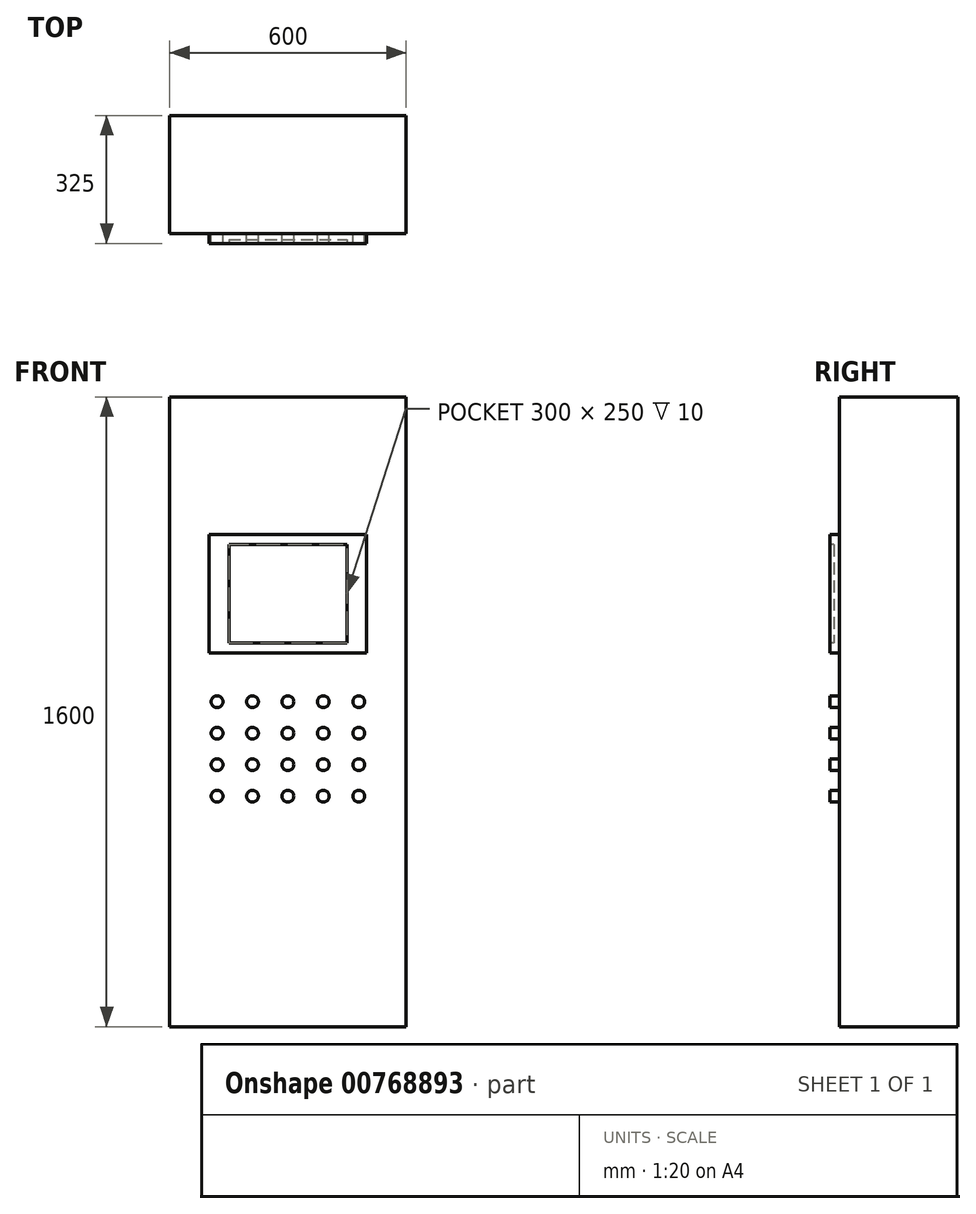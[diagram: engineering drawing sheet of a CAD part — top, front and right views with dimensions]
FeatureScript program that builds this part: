
annotation { "Feature Type Name" : "Feature", "Feature Type Description" : "" }
export const myFeature = defineFeature(function(context is Context, id is Id, definition is map)
    precondition{}
    {
        {
            var Q0;
            Q0=qCreatedBy(makeId("Front.planeOp"),FACE);
            var sketch = newSketch(context, id + "F0", { "sketchPlane" : qUnion([Q0])});
            skLineSegment(sketch, "E0.bottom", {"start": v(0, 0) * mm, "end": v(600, 0) * mm});
            skLineSegment(sketch, "E0.top", {"start": v(0, 1600) * mm, "end": v(600, 1600) * mm});
            skLineSegment(sketch, "E0.left", {"start": v(0, 0) * mm, "end": v(0, 1600) * mm});
            skLineSegment(sketch, "E0.right", {"start": v(600, 0) * mm, "end": v(600, 1600) * mm});
            skSolve(sketch);
        }
        {
            var Q0;
            Q0=makeQuery(id+"F0.imprint","IMPRINT",FACE,{"disambiguationData":[TD([[makeQuery(id+"F0.imprint","IMPRINT",EDGE,{"derivedFrom":sQuery(id+"F0.wireOp",EDGE,"E0.bottom")}),1.0]])]});
            extrude(context, id + "F1", {"entities" : qUnion([Q0]), "depth" : 300 * mm, "offsetDistance" : 25 * mm});
        }
        {
            var Q0;
            Q0=makeQuery(id+"F1.opExtrude","CAP_FACE",FACE,{"disambiguationData":[OSD([sQuery(id+"F0.wireOp",EDGE,"E0.bottom"),sQuery(id+"F0.wireOp",EDGE,"E0.top"),sQuery(id+"F0.wireOp",EDGE,"E0.left"),sQuery(id+"F0.wireOp",EDGE,"E0.right")])],"isStart":false});
            var sketch = newSketch(context, id + "F2", { "sketchPlane" : qUnion([Q0])});
            skLineSegment(sketch, "E1.bottom", {"start": v(100, 1250) * mm, "end": v(500, 1250) * mm});
            skLineSegment(sketch, "E1.top", {"start": v(100, 950) * mm, "end": v(500, 950) * mm});
            skLineSegment(sketch, "E1.left", {"start": v(100, 1250) * mm, "end": v(100, 950) * mm});
            skLineSegment(sketch, "E1.right", {"start": v(500, 1250) * mm, "end": v(500, 950) * mm});
            skSolve(sketch);
        }
        {
            var Q0;
            Q0=makeQuery(id+"F2.imprint","IMPRINT",FACE,{"disambiguationData":[TD([[makeQuery(id+"F2.imprint","IMPRINT",EDGE,{"derivedFrom":sQuery(id+"F2.wireOp",EDGE,"E1.bottom")}),-1.0]])]});
            extrude(context, id + "F3", {"entities" : qUnion([Q0]), "operationType" : NewBodyOperationType.ADD, "depth" : 25 * mm, "offsetDistance" : 25 * mm});
        }
        {
            var Q0;
            Q0=makeQuery(id+"F3.opExtrude","CAP_FACE",FACE,{"disambiguationData":[OSD([sQuery(id+"F2.wireOp",EDGE,"E1.bottom"),sQuery(id+"F2.wireOp",EDGE,"E1.top"),sQuery(id+"F2.wireOp",EDGE,"E1.left"),sQuery(id+"F2.wireOp",EDGE,"E1.right")])],"isStart":false});
            var sketch = newSketch(context, id + "F4", { "sketchPlane" : qUnion([Q0])});
            skLineSegment(sketch, "E2.bottom", {"start": v(150, 1225) * mm, "end": v(450, 1225) * mm});
            skLineSegment(sketch, "E2.top", {"start": v(150, 975) * mm, "end": v(450, 975) * mm});
            skLineSegment(sketch, "E2.left", {"start": v(150, 1225) * mm, "end": v(150, 975) * mm});
            skLineSegment(sketch, "E2.right", {"start": v(450, 1225) * mm, "end": v(450, 975) * mm});
            skSolve(sketch);
        }
        {
            var Q0;
            Q0=makeQuery(id+"F4.imprint","IMPRINT",FACE,{"disambiguationData":[TD([[makeQuery(id+"F4.imprint","IMPRINT",EDGE,{"derivedFrom":sQuery(id+"F4.wireOp",EDGE,"E2.bottom")}),-1.0]])]});
            extrude(context, id + "F5", {"entities" : qUnion([Q0]), "operationType" : NewBodyOperationType.REMOVE, "oppositeDirection" : true, "depth" : 10 * mm, "offsetDistance" : 25 * mm});
        }
        {
            var Q0;
            Q0=makeQuery(id+"F1.opExtrude","CAP_FACE",FACE,{"disambiguationData":[OSD([sQuery(id+"F0.wireOp",EDGE,"E0.bottom"),sQuery(id+"F0.wireOp",EDGE,"E0.top"),sQuery(id+"F0.wireOp",EDGE,"E0.left"),sQuery(id+"F0.wireOp",EDGE,"E0.right")])],"isStart":false});
            var sketch = newSketch(context, id + "F6", { "sketchPlane" : qUnion([Q0])});
            skCircle(sketch, "E3", {"center": v(120, 825.67) * mm, "radius": 15 * mm});
            skCircle(sketch, "E4.0.1.0", {"center": v(120, 745.67) * mm, "radius": 15 * mm});
            skCircle(sketch, "E4.0.2.0", {"center": v(120, 665.67) * mm, "radius": 15 * mm});
            skCircle(sketch, "E4.0.3.0", {"center": v(120, 585.67) * mm, "radius": 15 * mm});
            skCircle(sketch, "E4.1.0.0", {"center": v(210, 825.67) * mm, "radius": 15 * mm});
            skCircle(sketch, "E4.1.1.0", {"center": v(210, 745.67) * mm, "radius": 15 * mm});
            skCircle(sketch, "E4.1.2.0", {"center": v(210, 665.67) * mm, "radius": 15 * mm});
            skCircle(sketch, "E4.1.3.0", {"center": v(210, 585.67) * mm, "radius": 15 * mm});
            skCircle(sketch, "E4.2.0.0", {"center": v(300, 825.67) * mm, "radius": 15 * mm});
            skCircle(sketch, "E4.2.1.0", {"center": v(300, 745.67) * mm, "radius": 15 * mm});
            skCircle(sketch, "E4.2.2.0", {"center": v(300, 665.67) * mm, "radius": 15 * mm});
            skCircle(sketch, "E4.2.3.0", {"center": v(300, 585.67) * mm, "radius": 15 * mm});
            skCircle(sketch, "E4.3.0.0", {"center": v(390, 825.67) * mm, "radius": 15 * mm});
            skCircle(sketch, "E4.3.1.0", {"center": v(390, 745.67) * mm, "radius": 15 * mm});
            skCircle(sketch, "E4.3.2.0", {"center": v(390, 665.67) * mm, "radius": 15 * mm});
            skCircle(sketch, "E4.3.3.0", {"center": v(390, 585.67) * mm, "radius": 15 * mm});
            skCircle(sketch, "E4.4.0.0", {"center": v(480, 825.67) * mm, "radius": 15 * mm});
            skCircle(sketch, "E4.4.1.0", {"center": v(480, 745.67) * mm, "radius": 15 * mm});
            skCircle(sketch, "E4.4.2.0", {"center": v(480, 665.67) * mm, "radius": 15 * mm});
            skCircle(sketch, "E4.4.3.0", {"center": v(480, 585.67) * mm, "radius": 15 * mm});
            skLineSegment(sketch, "E4.direction1", {"start": v(120, 825.67) * mm, "end": v(210, 825.67) * mm, "construction": true});
            skLineSegment(sketch, "E4.direction2", {"start": v(120, 825.67) * mm, "end": v(120, 745.67) * mm, "construction": true});
            skSolve(sketch);
        }
        {
            var Q0;
            Q0 = qSketchRegion(id + "F6", true);
            extrude(context, id + "F7", {"entities" : qUnion([Q0]), "depth" : 25 * mm, "offsetDistance" : 25 * mm});
        }
    });
